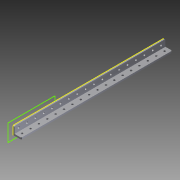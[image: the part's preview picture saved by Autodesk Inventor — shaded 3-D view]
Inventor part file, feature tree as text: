
AUTODESK INVENTOR PART (.ipt)
format: ipt  version: 2013 (Build 170138000, 138)  size: 152,576 bytes
history: native  units: in
note: dims shown in document units (in); Inventor stores cm internally (conversion verified against a paired STEP export)
features: other x1, imported_body x1, sketch x1
ambient origin geometry x8: Origin, YZ Plane, XZ Plane, XY Plane, X Axis, Y Axis, Z Axis, Center Point
feature tree (3):
  other  "ANGLE_288_2011"
  imported_body  "Base1"
  sketch  "Sketch1"
